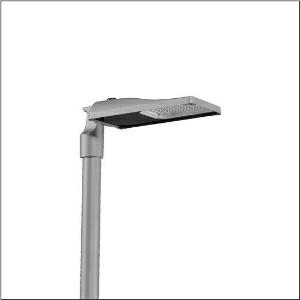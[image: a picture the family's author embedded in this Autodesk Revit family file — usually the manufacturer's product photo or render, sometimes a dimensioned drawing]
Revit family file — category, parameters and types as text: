
# Revit family: streetlight_sl_31_mini___st1_0a_5xh6d31s08ga_35d4
name_source: partatom
category: Lighting Fixtures
units: mm (PartAtom-declared; Revit-internal decimal feet)

## family parameters
Cut with Voids When Loaded = No
Host = Face
Light Source = No
Part Type = Normal
Room Calculation Point = No
Round Connector Dimension = Use Diameter
Shared = No

## types (1)
- --- (1 x LED, 5880 lm, 39.3 W, 3000K)
    Apparent Load = 39 VA
    CIE Flux Codes = 37 72 97 100 100
    Color Rendering = 70
    Color Temperature = 3000K
    Default Elevation = 1800 mm
    Description = Streetlight SL 31 mini D4i, Desk-Remote mast luminaire for post-top, side-entry; light control with lens of PMMA; light distribution: ST1.0a, direct asymmetric distribution, for standard-compliant lighting for roads and squares; LED: luminous flux: 5.880lm, light colour: 730, colour temperature: 3000K; luminous efficacy: 149,6lm/W; control: pre-setting: logarithmic dimming characteristic, flexible luminous flux parameterisation, time-dependent luminous flux control, constant luminous flux control, power reduction, intelligent temperature release in ECG and LED module, overheat protection; luminaire housing, of diecast aluminium, SITECO metallic grey (DB 702S), corrosivity category C5 high according to DIN EN ISO 12944; cover of toughened safety glass, transparent, opened without tools; mast flange of diecast aluminium, SITECO metallic grey (DB 702S), spigot size: 76/60mm, mast flange included unmounted; with cable H07RN-F 2x 1.5mm², cable length: 6,5m, connection cable pre-assembled; mains connection: 220..240V, AC, 50/60Hz; power consumption (at start of service life): 39,3W / (at end of service life): 40,7W / (with reduced operation 50%): 18,1W; protection rating (complete): IP66; insulation class (complete): insulation class II (safety insulation); impact resistance: IK10; certification: CE, ENEC, ENEC+, VDE, UKCA, ZD4i; permissible operating ambient temperature for outdoor applications: -40..+50°C; packaging unit: 1 piece

Light Distribution: ST1.0a
    Height = 76 mm
    Lamp = 1 x LED
    Lamp Light Flux = 5880 lm
    Lamp Power = 39.3 W
    Lamp count = 1
    Length = 547 mm
    Luminous efficacy = 150 lm/W
    Manufacturer = Siteco
    ModVariant = No
    Model = 5XH6D31S08GA
    Number of Poles = 1
    OnlyDefault = Yes
    Power Factor = 1
    Product Name = Streetlight SL 31 mini | ST1.0a
    Product group = mast luminaire | pylon top
    ProductGroupID = 6100
    Protection Class = Protection class II
    Protection Degree = IP 66
    RLX_Detail_Level = 1
    RLX_Emergency_Light_Flux = 0 lm
    RLX_Emergency_Type = 0
    RLX_Emergency_Type_DB = No
    RlxData = <blob elided: 39589 chars, md5=23d59b76>
    Socket = socket
    Standby Power = 0 W
    System Light Flux = 5880 lm
    System Power = 39 W
    Type Comments = factory setting: luminous flux: 100 % | dim-lin: 254 | 798 mA
    Type Image = l_1300330.jpg
    URL = http://relux.com
    VarID = @adj_060705
    Voltage = 0 V
    Weight = 0.00 kg
    Width = 265 mm

## geometry (parser evidence)
native form markers: Blend x4, Sweep x11
no freeform markers — native parametric forms only
